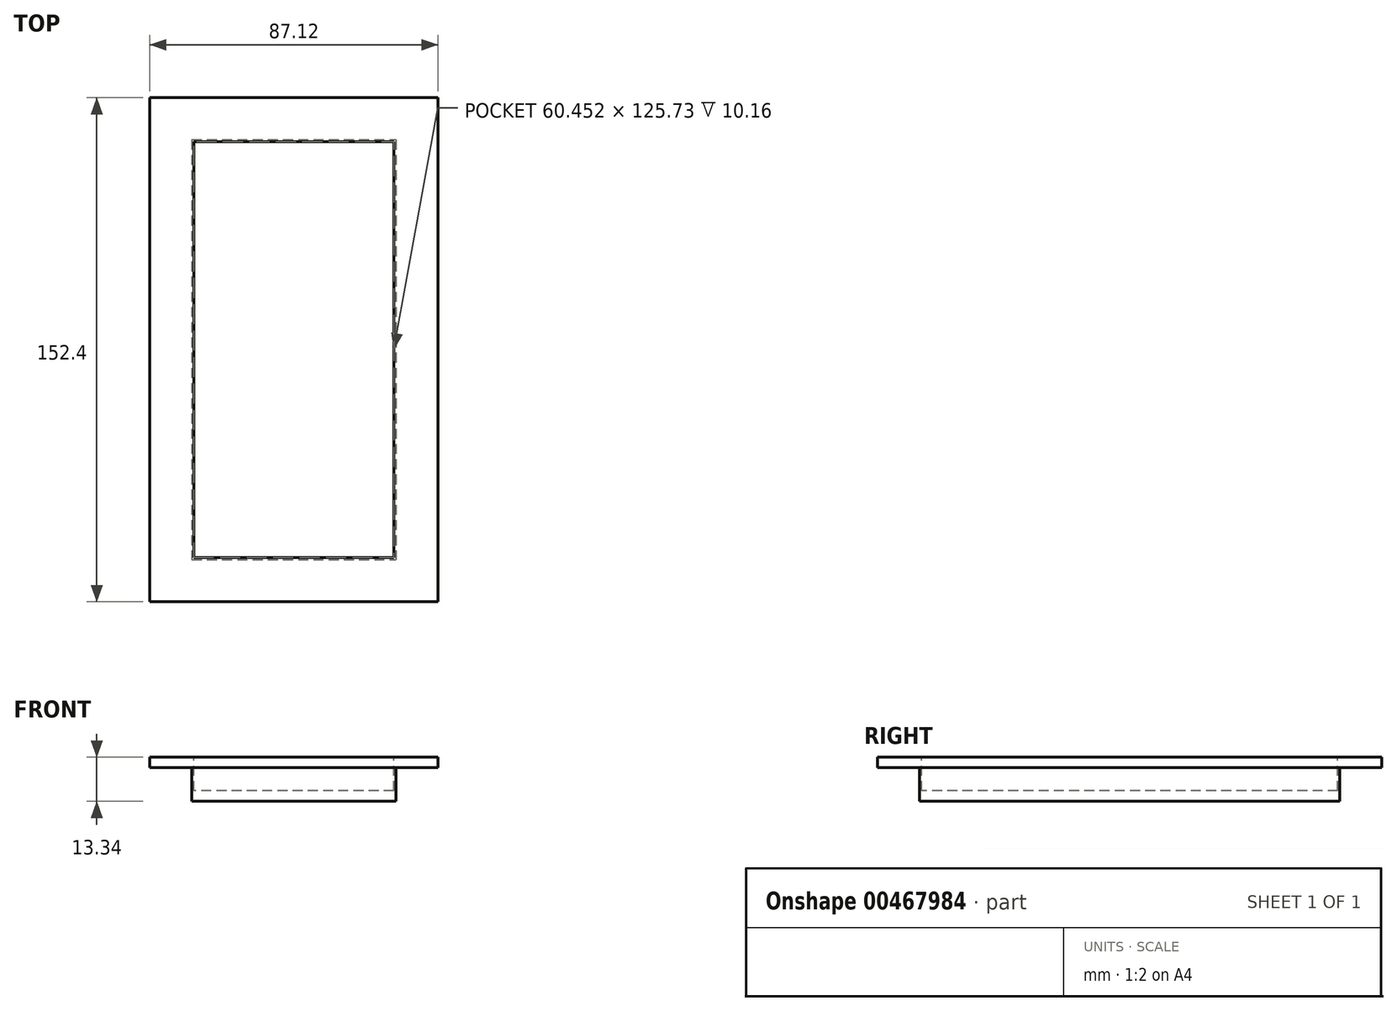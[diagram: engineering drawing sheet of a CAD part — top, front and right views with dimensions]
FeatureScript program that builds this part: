
annotation { "Feature Type Name" : "Feature", "Feature Type Description" : "" }
export const myFeature = defineFeature(function(context is Context, id is Id, definition is map)
    precondition{}
    {
        {
            var Q0;
            Q0=qCreatedBy(makeId("Top.planeOp"),FACE);
            var sketch = newSketch(context, id + "F0", { "sketchPlane" : qUnion([Q0])});
            skLineSegment(sketch, "E0.bottom", {"start": v(-30.86, 63.5) * mm, "end": v(30.86, 63.5) * mm});
            skLineSegment(sketch, "E0.top", {"start": v(-30.86, -63.5) * mm, "end": v(30.86, -63.5) * mm});
            skLineSegment(sketch, "E0.left", {"start": v(-30.86, 63.5) * mm, "end": v(-30.86, -63.5) * mm});
            skLineSegment(sketch, "E0.right", {"start": v(30.86, 63.5) * mm, "end": v(30.86, -63.5) * mm});
            skPoint(sketch, "E0.middle", {"position": v(0, 0) * mm});
            skSolve(sketch);
        }
        {
            var Q0;
            Q0 = qSketchRegion(id + "F0", true);
            extrude(context, id + "F1", {"entities" : qUnion([Q0]), "depth" : 10.16 * mm});
        }
        {
            var Q0;
            Q0=makeQuery(id+"F1.opExtrude","CAP_FACE",FACE,{"disambiguationData":[OSD([sQuery(id+"F0.wireOp",EDGE,"E0.bottom"),sQuery(id+"F0.wireOp",EDGE,"E0.top"),sQuery(id+"F0.wireOp",EDGE,"E0.left"),sQuery(id+"F0.wireOp",EDGE,"E0.right")])],"isStart":false});
            var sketch = newSketch(context, id + "F2", { "sketchPlane" : qUnion([Q0])});
            skLineSegment(sketch, "E1.bottom", {"start": v(43.56, 76.2) * mm, "end": v(-43.56, 76.2) * mm});
            skLineSegment(sketch, "E1.top", {"start": v(43.56, -76.2) * mm, "end": v(-43.56, -76.2) * mm});
            skLineSegment(sketch, "E1.left", {"start": v(43.56, 76.2) * mm, "end": v(43.56, -76.2) * mm});
            skLineSegment(sketch, "E1.right", {"start": v(-43.56, 76.2) * mm, "end": v(-43.56, -76.2) * mm});
            skPoint(sketch, "E1.middle", {"position": v(0, 0) * mm});
            skSolve(sketch);
        }
        {
            var Q0;
            Q0 = qSketchRegion(id + "F2", true);
            extrude(context, id + "F3", {"entities" : qUnion([Q0]), "operationType" : NewBodyOperationType.ADD, "depth" : 3.17 * mm});
        }
        {
            var Q0;
            Q0=makeQuery(id+"F3.opExtrude","CAP_FACE",FACE,{"disambiguationData":[OSD([sQuery(id+"F2.wireOp",EDGE,"E1.bottom"),sQuery(id+"F2.wireOp",EDGE,"E1.top"),sQuery(id+"F2.wireOp",EDGE,"E1.left"),sQuery(id+"F2.wireOp",EDGE,"E1.right")])],"isStart":false});
            var sketch = newSketch(context, id + "F4", { "sketchPlane" : qUnion([Q0])});
            skLineSegment(sketch, "E2.bottom", {"start": v(30.23, 62.87) * mm, "end": v(-30.23, 62.87) * mm});
            skLineSegment(sketch, "E2.top", {"start": v(30.23, -62.87) * mm, "end": v(-30.23, -62.87) * mm});
            skLineSegment(sketch, "E2.left", {"start": v(30.23, 62.87) * mm, "end": v(30.23, -62.87) * mm});
            skLineSegment(sketch, "E2.right", {"start": v(-30.23, 62.87) * mm, "end": v(-30.23, -62.87) * mm});
            skPoint(sketch, "E2.middle", {"position": v(0, 0) * mm});
            skSolve(sketch);
        }
        {
            var Q0;
            Q0=makeQuery(id+"F4.imprint","IMPRINT",FACE,{"disambiguationData":[TD([[makeQuery(id+"F4.imprint","IMPRINT",EDGE,{"derivedFrom":sQuery(id+"F4.wireOp",EDGE,"E2.bottom")}),1.0]])]});
            extrude(context, id + "F5", {"entities" : qUnion([Q0]), "operationType" : NewBodyOperationType.REMOVE, "oppositeDirection" : true, "depth" : 10.16 * mm});
        }
    });
